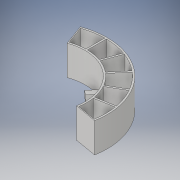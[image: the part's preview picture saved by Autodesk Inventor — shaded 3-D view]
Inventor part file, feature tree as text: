
AUTODESK INVENTOR PART (.ipt)
format: ipt  version: 2019 (Build 230136000, 136)  size: 335,360 bytes
history: native  units: mm
features: extrude x3, sketch x2, pattern_circular x1, other x1, mirror x1
ambient origin geometry x8: Origin, YZ Plane, XZ Plane, XY Plane, X Axis, Y Axis, Z Axis, Center Point
bodies: Solide1 (feature_tree)
feature tree (8):
  sketch  "Esquisse1"
  extrude  "Extrusion2"  Depth=200.0mm
  extrude  "Extrusion3"  Depth=1.745329mm
  pattern_circular  "Réseau circulaire1"  [2 undecoded]
  extrude  "Extrusion4"  Depth=40.0mm
  other  "Plan de construction1"
  mirror  "Symétrie1"
  sketch  "Esquisse2"
note: 2 required parameter values undecoded (feature->parameter linkage not recoverable at this tier; creation-order binding heuristic only, values carry confidence <= 0.55)
